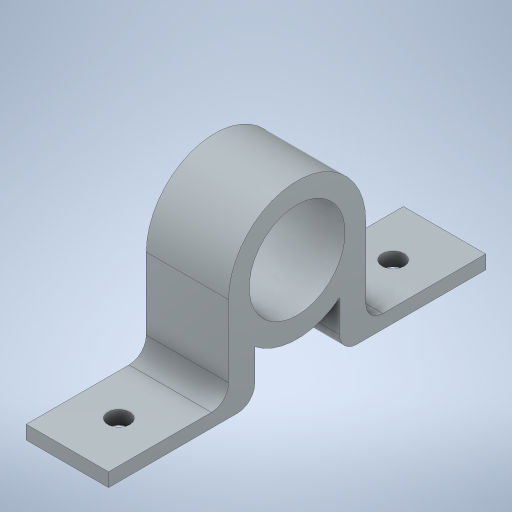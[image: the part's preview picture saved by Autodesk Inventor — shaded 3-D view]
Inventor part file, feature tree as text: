
AUTODESK INVENTOR PART (.ipt)
format: ipt  version: 2024 (Build 280153020, 153B)  size: 291,328 bytes
history: native  units: mm
features: extrude x3, sketch x3
ambient origin geometry x8: Origin, YZ Plane, XZ Plane, XY Plane, X Axis, Y Axis, Z Axis, Center Point
bodies: Solid1 (feature_tree)
feature tree (6):
  extrude  "Extrusion1"  Depth=3.0mm
  extrude  "Extrusion2"  Depth=2.5mm
  extrude  "Extrusion3"  Depth=12.0mm
  sketch  "Sketch1"  dims[d0=14.0mm d1=3.0mm]
  sketch  "Sketch2"  dims[d2=13.0mm d4=2.5mm]
  sketch  "Sketch3"  dims[d5=12.0mm d6=0.0mm d7=15.0mm d8=3.2mm d9=12.0mm d10=0.0mm d11=3.2mm d12=12.0mm d13=0.0mm]
